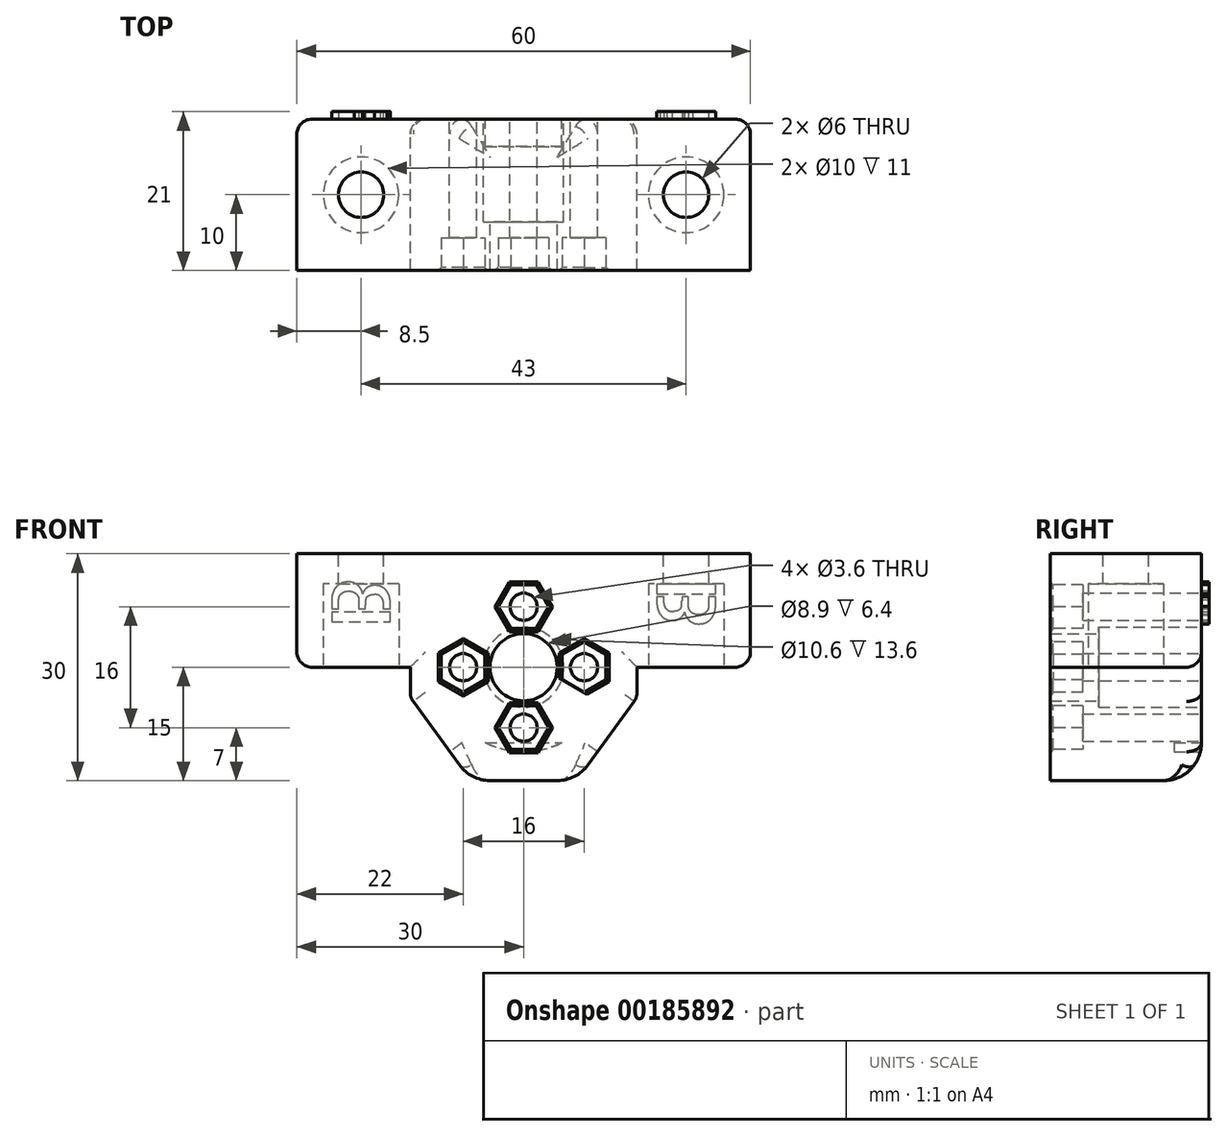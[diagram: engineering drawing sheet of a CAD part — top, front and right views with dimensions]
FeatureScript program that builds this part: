
annotation { "Feature Type Name" : "Feature", "Feature Type Description" : "" }
export const myFeature = defineFeature(function(context is Context, id is Id, definition is map)
    precondition{}
    {
        {
            var Q0;
            Q0=qCreatedBy(makeId("Front.planeOp"),FACE);
            var sketch = newSketch(context, id + "F0", { "sketchPlane" : qUnion([Q0])});
            skLineSegment(sketch, "E0.bottom", {"start": v(30, -7.5) * mm, "end": v(-30, -7.5) * mm});
            skLineSegment(sketch, "E0.top", {"start": v(30, 7.5) * mm, "end": v(-30, 7.5) * mm});
            skLineSegment(sketch, "E0.left", {"start": v(30, -7.5) * mm, "end": v(30, 7.5) * mm});
            skLineSegment(sketch, "E0.right", {"start": v(-30, -7.5) * mm, "end": v(-30, 7.5) * mm});
            skPoint(sketch, "E0.middle", {"position": v(0, 0) * mm});
            skLineSegment(sketch, "E1.bottom", {"start": v(-15, -7.5) * mm, "end": v(15, -7.5) * mm});
            skLineSegment(sketch, "E1.top", {"start": v(-15, -22.5) * mm, "end": v(15, -22.5) * mm});
            skLineSegment(sketch, "E1.left", {"start": v(-15, -7.5) * mm, "end": v(-15, -22.5) * mm});
            skLineSegment(sketch, "E1.right", {"start": v(15, -7.5) * mm, "end": v(15, -22.5) * mm});
            skPoint(sketch, "E2", {"position": v(0, -7.5) * mm});
            skCircle(sketch, "E3", {"center": v(0, -7.5) * mm, "radius": 4.45 * mm});
            skLineSegment(sketch, "E4", {"start": v(-7, -22.5) * mm, "end": v(-15, -11.5) * mm});
            skLineSegment(sketch, "E5.MirrorCS", {"start": v(7, -22.5) * mm, "end": v(15, -11.5) * mm});
            skLineSegment(sketch, "E6.MirrorCS", {"start": v(15, -22.5) * mm, "end": v(-15, -22.5) * mm});
            skSolve(sketch);
        }
        {
            var Q0;
            {var subQ10=sQuery(id+"F0.wireOp",EDGE,"E4");Q0=makeQuery(id+"F0.imprint","IMPRINT",FACE,{"disambiguationData":[TD([[makeQuery(id+"F0.imprint","IMPRINT",EDGE,{"derivedFrom":subQ10}),-1.0]])]});}
            var Q1;
            Q1=makeQuery(id+"F0.imprint","IMPRINT",FACE,{"disambiguationData":[TD([[makeQuery(id+"F0.imprint","IMPRINT",EDGE,{"derivedFrom":sQuery(id+"F0.wireOp",EDGE,"E0.top")}),1.0]])]});
            extrude(context, id + "F1", {"entities" : qUnion([Q0, Q1]), "depth" : 20 * mm});
        }
        {
            var Q0;
            Q0=makeQuery(id+"F1.opExtrude","SWEPT_FACE",FACE,{"disambiguationData":[OSD([sQuery(id+"F0.wireOp",EDGE,"E0.top")])]});
            var sketch = newSketch(context, id + "F2", { "sketchPlane" : qUnion([Q0])});
            skCircle(sketch, "E7", {"center": v(-21.5, -10) * mm, "radius": 3 * mm});
            skCircle(sketch, "E8.MirrorC", {"center": v(21.5, -10) * mm, "radius": 3 * mm});
            skSolve(sketch);
        }
        {
            var Q0;
            Q0 = qSketchRegion(id + "F2", true);
            extrude(context, id + "F3", {"entities" : qUnion([Q0]), "operationType" : NewBodyOperationType.REMOVE, "endBound" : BoundingType.UP_TO_NEXT, "oppositeDirection" : true, "depth" : 25 * mm});
        }
        {
            var Q0;
            {var subQ0=sQuery(id+"F0.wireOp",EDGE,"E0.bottom");Q0=makeQuery(id+"F1.opExtrude","SWEPT_FACE",FACE,{"disambiguationData":[OSD([subQ0]),TDD([makeQuery(id+"F0.imprint","IMPRINT",EDGE,{"disambiguationData":[TD([[makeQuery(id+"F0.imprint","INTERSECT",VERTEX,{"derivedFrom":[subQ0,sQuery(id+"F0.wireOp",EDGE,"E0.right")]}),1.0]])],"derivedFrom":subQ0})])]});}
            var sketch = newSketch(context, id + "F4", { "sketchPlane" : qUnion([Q0])});
            skCircle(sketch, "E9", {"center": v(-21.5, 10) * mm, "radius": 5 * mm});
            skCircle(sketch, "E10.MirrorC", {"center": v(21.5, 10) * mm, "radius": 5 * mm});
            skSolve(sketch);
        }
        {
            var Q0;
            Q0 = qSketchRegion(id + "F4", true);
            extrude(context, id + "F5", {"entities" : qUnion([Q0]), "operationType" : NewBodyOperationType.REMOVE, "oppositeDirection" : true, "depth" : 11 * mm});
        }
        {
            var Q0;
            {var subQ0=sQuery(id+"F0.wireOp",EDGE,"E0.bottom");Q0=makeQuery(id+"F1.opExtrude","CAP_EDGE",EDGE,{"disambiguationData":[OSD([subQ0]),TDD([makeQuery(id+"F0.imprint","IMPRINT",EDGE,{"disambiguationData":[TD([[makeQuery(id+"F0.imprint","INTERSECT",VERTEX,{"derivedFrom":[subQ0,sQuery(id+"F0.wireOp",EDGE,"E0.right")]}),1.0]])],"derivedFrom":subQ0})])],"isStart":true});}
            var Q1;
            Q1=makeQuery(id+"F1.opExtrude","CAP_EDGE",EDGE,{"disambiguationData":[OSD([sQuery(id+"F0.wireOp",EDGE,"E0.right")])],"isStart":true});
            var Q2;
            Q2=makeQuery(id+"F1.opExtrude","CAP_EDGE",EDGE,{"disambiguationData":[OSD([sQuery(id+"F0.wireOp",EDGE,"E1.left")])],"isStart":true});
            var Q3;
            Q3=makeQuery(id+"F1.opExtrude","CAP_EDGE",EDGE,{"disambiguationData":[OSD([sQuery(id+"F0.wireOp",EDGE,"E4")])],"isStart":true});
            var Q4;
            Q4=makeQuery(id+"F1.opExtrude","CAP_EDGE",EDGE,{"disambiguationData":[OSD([sQuery(id+"F0.wireOp",EDGE,"E6.MirrorCS")])],"isStart":true});
            var Q5;
            Q5=makeQuery(id+"F1.opExtrude","CAP_EDGE",EDGE,{"disambiguationData":[OSD([sQuery(id+"F0.wireOp",EDGE,"E5.MirrorCS")])],"isStart":true});
            var Q6;
            Q6=makeQuery(id+"F1.opExtrude","CAP_EDGE",EDGE,{"disambiguationData":[OSD([sQuery(id+"F0.wireOp",EDGE,"E1.right")])],"isStart":true});
            var Q7;
            {var subQ0=sQuery(id+"F0.wireOp",EDGE,"E0.bottom");Q7=makeQuery(id+"F1.opExtrude","CAP_EDGE",EDGE,{"disambiguationData":[OSD([subQ0]),TDD([makeQuery(id+"F0.imprint","IMPRINT",EDGE,{"disambiguationData":[TD([[makeQuery(id+"F0.imprint","INTERSECT",VERTEX,{"derivedFrom":[subQ0,sQuery(id+"F0.wireOp",EDGE,"E0.left")]}),-1.0]])],"derivedFrom":subQ0})])],"isStart":true});}
            var Q8;
            Q8=makeQuery(id+"F1.opExtrude","CAP_EDGE",EDGE,{"disambiguationData":[OSD([sQuery(id+"F0.wireOp",EDGE,"E0.left")])],"isStart":true});
            var Q9;
            Q9=makeQuery(id+"F1.opExtrude","SWEPT_EDGE",EDGE,{"disambiguationData":[OSD([sQuery(id+"F0.wireOp",EDGE,"E1.right"),sQuery(id+"F0.wireOp",EDGE,"E5.MirrorCS")])]});
            var Q10;
            Q10=makeQuery(id+"F1.opExtrude","SWEPT_EDGE",EDGE,{"disambiguationData":[OSD([sQuery(id+"F0.wireOp",EDGE,"E1.left"),sQuery(id+"F0.wireOp",EDGE,"E4")])]});
            var Q11;
            Q11=makeQuery(id+"F1.opExtrude","SWEPT_EDGE",EDGE,{"disambiguationData":[OSD([sQuery(id+"F0.wireOp",EDGE,"E0.bottom"),sQuery(id+"F0.wireOp",EDGE,"E0.right")])]});
            var Q12;
            Q12=makeQuery(id+"F1.opExtrude","SWEPT_EDGE",EDGE,{"disambiguationData":[OSD([sQuery(id+"F0.wireOp",EDGE,"E0.bottom"),sQuery(id+"F0.wireOp",EDGE,"E0.left")])]});
            fillet(context, id + "F6", {"entities" : qUnion([Q0, Q1, Q2, Q3, Q4, Q5, Q6, Q7, Q8, Q9, Q10, Q11, Q12]), "radius" : 2 * mm, "tangentPropagation" : true});
        }
        {
            var Q0;
            Q0=makeQuery(id+"F1.opExtrude","SWEPT_EDGE",EDGE,{"disambiguationData":[OSD([sQuery(id+"F0.wireOp",EDGE,"E4"),sQuery(id+"F0.wireOp",EDGE,"E6.MirrorCS")])]});
            var Q1;
            Q1=makeQuery(id+"F1.opExtrude","SWEPT_EDGE",EDGE,{"disambiguationData":[OSD([sQuery(id+"F0.wireOp",EDGE,"E5.MirrorCS"),sQuery(id+"F0.wireOp",EDGE,"E6.MirrorCS")])]});
            fillet(context, id + "F7", {"entities" : qUnion([Q0, Q1]), "radius" : 5 * mm, "tangentPropagation" : true});
        }
        {
            var Q0;
            Q0=makeQuery(id+"F1.opExtrude","CAP_FACE",FACE,{"disambiguationData":[OSD([sQuery(id+"F0.wireOp",EDGE,"E0.bottom"),sQuery(id+"F0.wireOp",EDGE,"E0.top"),sQuery(id+"F0.wireOp",EDGE,"E0.left"),sQuery(id+"F0.wireOp",EDGE,"E0.right"),sQuery(id+"F0.wireOp",EDGE,"E1.left"),sQuery(id+"F0.wireOp",EDGE,"E3"),sQuery(id+"F0.wireOp",EDGE,"E4"),sQuery(id+"F0.wireOp",EDGE,"E1.right"),sQuery(id+"F0.wireOp",EDGE,"E5.MirrorCS"),sQuery(id+"F0.wireOp",EDGE,"E6.MirrorCS")])],"isStart":true});
            var sketch = newSketch(context, id + "F8", { "sketchPlane" : qUnion([Q0])});
            skCircle(sketch, "E11", {"center": v(0, -7.5) * mm, "radius": 11.2 * mm});
            skCircle(sketch, "E12", {"center": v(0, -7.5) * mm, "radius": 5.3 * mm});
            skCircle(sketch, "E13", {"center": v(8, -7.5) * mm, "radius": 1.8 * mm});
            skCircle(sketch, "E14.1.0", {"center": v(0, 0.5) * mm, "radius": 1.8 * mm});
            skCircle(sketch, "E14.2.0", {"center": v(-8, -7.5) * mm, "radius": 1.8 * mm});
            skCircle(sketch, "E14.3.0", {"center": v(0, -15.5) * mm, "radius": 1.8 * mm});
            skCircle(sketch, "E15", {"center": v(0, -7.5) * mm, "radius": 8 * mm, "construction": true});
            skSolve(sketch);
        }
        {
            var Q0;
            Q0=makeQuery(id+"F8.imprint","IMPRINT",FACE,{"disambiguationData":[TD([[makeQuery(id+"F8.imprint","IMPRINT",EDGE,{"derivedFrom":sQuery(id+"F8.wireOp",EDGE,"E12")}),1.0]])]});
            var Q1;
            Q1=makeQuery(id+"F8.imprint","IMPRINT",FACE,{"disambiguationData":[TD([[makeQuery(id+"F8.imprint","IMPRINT",EDGE,{"derivedFrom":makeQuery(id+"F1.opExtrude","CAP_EDGE",EDGE,{"disambiguationData":[OSD([sQuery(id+"F0.wireOp",EDGE,"E3")])],"isStart":true})}),-1.0]])]});
            extrude(context, id + "F9", {"entities" : qUnion([Q0, Q1]), "operationType" : NewBodyOperationType.REMOVE, "oppositeDirection" : true, "depth" : (3.6 + 10) * mm});
        }
        {
            var Q0;
            Q0=makeQuery(id+"F8.imprint","IMPRINT",FACE,{"disambiguationData":[TD([[makeQuery(id+"F8.imprint","IMPRINT",EDGE,{"derivedFrom":sQuery(id+"F8.wireOp",EDGE,"E11")}),1.0]])]});
            var Q1;
            Q1=makeQuery(id+"F8.imprint","IMPRINT",FACE,{"disambiguationData":[TD([[makeQuery(id+"F8.imprint","IMPRINT",EDGE,{"derivedFrom":sQuery(id+"F8.wireOp",EDGE,"E13")}),1.0]])]});
            var Q2;
            Q2=makeQuery(id+"F8.imprint","IMPRINT",FACE,{"disambiguationData":[TD([[makeQuery(id+"F8.imprint","IMPRINT",EDGE,{"derivedFrom":sQuery(id+"F8.wireOp",EDGE,"E14.3.0")}),1.0]])]});
            var Q3;
            Q3=makeQuery(id+"F8.imprint","IMPRINT",FACE,{"disambiguationData":[TD([[makeQuery(id+"F8.imprint","IMPRINT",EDGE,{"derivedFrom":sQuery(id+"F8.wireOp",EDGE,"E14.2.0")}),1.0]])]});
            var Q4;
            Q4=makeQuery(id+"F8.imprint","IMPRINT",FACE,{"disambiguationData":[TD([[makeQuery(id+"F8.imprint","IMPRINT",EDGE,{"derivedFrom":sQuery(id+"F8.wireOp",EDGE,"E14.1.0")}),1.0]])]});
            extrude(context, id + "F10", {"entities" : qUnion([Q0, Q1, Q2, Q3, Q4]), "operationType" : NewBodyOperationType.REMOVE, "oppositeDirection" : true, "depth" : (3.5 + .1) * mm});
        }
        {
            var Q0;
            Q0=makeQuery(id+"F8.imprint","IMPRINT",FACE,{"disambiguationData":[TD([[makeQuery(id+"F8.imprint","IMPRINT",EDGE,{"derivedFrom":sQuery(id+"F8.wireOp",EDGE,"E13")}),1.0]])]});
            var Q1;
            Q1=makeQuery(id+"F8.imprint","IMPRINT",FACE,{"disambiguationData":[TD([[makeQuery(id+"F8.imprint","IMPRINT",EDGE,{"derivedFrom":sQuery(id+"F8.wireOp",EDGE,"E14.3.0")}),1.0]])]});
            var Q2;
            Q2=makeQuery(id+"F8.imprint","IMPRINT",FACE,{"disambiguationData":[TD([[makeQuery(id+"F8.imprint","IMPRINT",EDGE,{"derivedFrom":sQuery(id+"F8.wireOp",EDGE,"E14.2.0")}),1.0]])]});
            var Q3;
            Q3=makeQuery(id+"F8.imprint","IMPRINT",FACE,{"disambiguationData":[TD([[makeQuery(id+"F8.imprint","IMPRINT",EDGE,{"derivedFrom":sQuery(id+"F8.wireOp",EDGE,"E14.1.0")}),1.0]])]});
            var Q4;
            Q4=makeQuery(id+"F1.opExtrude","CAP_FACE",FACE,{"disambiguationData":[OSD([sQuery(id+"F0.wireOp",EDGE,"E0.bottom"),sQuery(id+"F0.wireOp",EDGE,"E0.top"),sQuery(id+"F0.wireOp",EDGE,"E0.left"),sQuery(id+"F0.wireOp",EDGE,"E0.right"),sQuery(id+"F0.wireOp",EDGE,"E1.left"),sQuery(id+"F0.wireOp",EDGE,"E3"),sQuery(id+"F0.wireOp",EDGE,"E4"),sQuery(id+"F0.wireOp",EDGE,"E1.right"),sQuery(id+"F0.wireOp",EDGE,"E5.MirrorCS"),sQuery(id+"F0.wireOp",EDGE,"E6.MirrorCS")])],"isStart":false});
            extrude(context, id + "F11", {"entities" : qUnion([Q0, Q1, Q2, Q3]), "operationType" : NewBodyOperationType.REMOVE, "endBound" : BoundingType.UP_TO_SURFACE, "oppositeDirection" : true, "endBoundEntityFace" : qUnion([Q4]), "depth" : 25 * mm});
        }
        {
            var Q0;
            Q0=makeQuery(id+"F1.opExtrude","CAP_FACE",FACE,{"disambiguationData":[OSD([sQuery(id+"F0.wireOp",EDGE,"E0.bottom"),sQuery(id+"F0.wireOp",EDGE,"E0.top"),sQuery(id+"F0.wireOp",EDGE,"E0.left"),sQuery(id+"F0.wireOp",EDGE,"E0.right"),sQuery(id+"F0.wireOp",EDGE,"E1.left"),sQuery(id+"F0.wireOp",EDGE,"E3"),sQuery(id+"F0.wireOp",EDGE,"E4"),sQuery(id+"F0.wireOp",EDGE,"E1.right"),sQuery(id+"F0.wireOp",EDGE,"E5.MirrorCS"),sQuery(id+"F0.wireOp",EDGE,"E6.MirrorCS")])],"isStart":true});
            var sketch = newSketch(context, id + "F12", { "sketchPlane" : qUnion([Q0])});
            skText(sketch, "E16", { "text": "B", "fontName": "AllertaStencil-Regular.ttf"});
            skLineSegment(sketch, "E17", {"start": v(21.5, 4.5) * mm, "end": v(21.5, -2.5) * mm, "construction": true});
            skLineSegment(sketch, "E18.MirrorCS", {"start": v(-21.5, 4.5) * mm, "end": v(-21.5, -2.5) * mm, "construction": true});
            skText(sketch, "E19", { "text": "B", "fontName": "AllertaStencil-Regular.ttf"});
            skLineSegment(sketch, "E20", {"start": v(-21.5, -2.5) * mm, "end": v(-21.5, 4.5) * mm, "construction": true});
            const initialGuessF12  = {"E16": [0.0254, -0.0025, 0, 1, 0.00779], "E19": [-0.0254, 0.0045, 0, -1, 0.00779]};
            skSetInitialGuess(sketch, initialGuessF12);
            skSolve(sketch);
        }
        {
            var Q0;
            Q0 = qSketchRegion(id + "F12", true);
            extrude(context, id + "F13", {"entities" : qUnion([Q0]), "operationType" : NewBodyOperationType.ADD, "depth" : 1 * mm});
        }
        {
            var Q0;
            Q0=makeQuery(id+"F1.opExtrude","CAP_FACE",FACE,{"disambiguationData":[OSD([sQuery(id+"F0.wireOp",EDGE,"E0.bottom"),sQuery(id+"F0.wireOp",EDGE,"E0.top"),sQuery(id+"F0.wireOp",EDGE,"E0.left"),sQuery(id+"F0.wireOp",EDGE,"E0.right"),sQuery(id+"F0.wireOp",EDGE,"E1.left"),sQuery(id+"F0.wireOp",EDGE,"E3"),sQuery(id+"F0.wireOp",EDGE,"E4"),sQuery(id+"F0.wireOp",EDGE,"E1.right"),sQuery(id+"F0.wireOp",EDGE,"E5.MirrorCS"),sQuery(id+"F0.wireOp",EDGE,"E6.MirrorCS")])],"isStart":false});
            var sketch = newSketch(context, id + "F14", { "sketchPlane" : qUnion([Q0])});
            skCircle(sketch, "E21.cCircle", {"center": v(0, -15.5) * mm, "radius": 2.9 * mm, "construction": true});
            skLineSegment(sketch, "E21.0", {"start": v(-1.67, -18.4) * mm, "end": v(-3.35, -15.5) * mm});
            skLineSegment(sketch, "E21.1", {"start": v(-3.35, -15.5) * mm, "end": v(-1.67, -12.6) * mm});
            skLineSegment(sketch, "E21.2", {"start": v(-1.67, -12.6) * mm, "end": v(1.67, -12.6) * mm});
            skLineSegment(sketch, "E21.3", {"start": v(1.67, -12.6) * mm, "end": v(3.35, -15.5) * mm});
            skLineSegment(sketch, "E21.4", {"start": v(3.35, -15.5) * mm, "end": v(1.67, -18.4) * mm});
            skLineSegment(sketch, "E21.5", {"start": v(1.67, -18.4) * mm, "end": v(-1.67, -18.4) * mm});
            skPoint(sketch, "E21.0.midPoint", {"position": v(-2.51, -16.95) * mm});
            skLineSegment(sketch, "E22", {"start": v(0, 0) * mm, "end": v(16.56, 0) * mm, "construction": true});
            skLineSegment(sketch, "E23.1.0", {"start": v(10.9, -5.83) * mm, "end": v(10.9, -9.17) * mm});
            skLineSegment(sketch, "E23.1.1", {"start": v(5.1, -9.17) * mm, "end": v(5.1, -5.83) * mm});
            skLineSegment(sketch, "E23.1.2", {"start": v(5.1, -5.83) * mm, "end": v(8, -4.15) * mm});
            skLineSegment(sketch, "E23.1.3", {"start": v(8, -10.85) * mm, "end": v(5.1, -9.17) * mm});
            skLineSegment(sketch, "E23.1.4", {"start": v(8, -4.15) * mm, "end": v(10.9, -5.83) * mm});
            skLineSegment(sketch, "E23.1.5", {"start": v(10.9, -9.17) * mm, "end": v(8, -10.85) * mm});
            skCircle(sketch, "E23.1.6", {"center": v(8, -7.5) * mm, "radius": 2.9 * mm, "construction": true});
            skPoint(sketch, "E23.1.7", {"position": v(9.45, -10.01) * mm});
            skLineSegment(sketch, "E23.2.0", {"start": v(-1.67, 3.4) * mm, "end": v(1.67, 3.4) * mm});
            skLineSegment(sketch, "E23.2.1", {"start": v(1.67, -2.4) * mm, "end": v(-1.67, -2.4) * mm});
            skLineSegment(sketch, "E23.2.2", {"start": v(-1.67, -2.4) * mm, "end": v(-3.35, 0.5) * mm});
            skLineSegment(sketch, "E23.2.3", {"start": v(3.35, 0.5) * mm, "end": v(1.67, -2.4) * mm});
            skLineSegment(sketch, "E23.2.4", {"start": v(-3.35, 0.5) * mm, "end": v(-1.67, 3.4) * mm});
            skLineSegment(sketch, "E23.2.5", {"start": v(1.67, 3.4) * mm, "end": v(3.35, 0.5) * mm});
            skCircle(sketch, "E23.2.6", {"center": v(0, 0.5) * mm, "radius": 2.9 * mm, "construction": true});
            skPoint(sketch, "E23.2.7", {"position": v(2.51, 1.95) * mm});
            skLineSegment(sketch, "E23.3.0", {"start": v(-10.9, -9.17) * mm, "end": v(-10.9, -5.83) * mm});
            skLineSegment(sketch, "E23.3.1", {"start": v(-5.1, -5.83) * mm, "end": v(-5.1, -9.17) * mm});
            skLineSegment(sketch, "E23.3.2", {"start": v(-5.1, -9.17) * mm, "end": v(-8, -10.85) * mm});
            skLineSegment(sketch, "E23.3.3", {"start": v(-8, -4.15) * mm, "end": v(-5.1, -5.83) * mm});
            skLineSegment(sketch, "E23.3.4", {"start": v(-8, -10.85) * mm, "end": v(-10.9, -9.17) * mm});
            skLineSegment(sketch, "E23.3.5", {"start": v(-10.9, -5.83) * mm, "end": v(-8, -4.15) * mm});
            skCircle(sketch, "E23.3.6", {"center": v(-8, -7.5) * mm, "radius": 2.9 * mm, "construction": true});
            skPoint(sketch, "E23.3.7", {"position": v(-9.45, -4.99) * mm});
            skPoint(sketch, "E23.center", {"position": v(0, -7.5) * mm});
            skSolve(sketch);
        }
        {
            var Q0;
            Q0 = qSketchRegion(id + "F14", true);
            extrude(context, id + "F15", {"entities" : qUnion([Q0]), "operationType" : NewBodyOperationType.REMOVE, "oppositeDirection" : true, "depth" : (4 + .3) * mm});
        }
        {
            var Q0;
            Q0=makeQuery(id+"F15.boolean.opBoolean","COPY",EDGE,{"derivedFrom":makeQuery(id+"F15.opExtrude","CAP_EDGE",EDGE,{"disambiguationData":[OSD([sQuery(id+"F14.wireOp",EDGE,"E23.3.0")])],"isStart":true})});
            var Q1;
            Q1=makeQuery(id+"F15.boolean.opBoolean","COPY",EDGE,{"derivedFrom":makeQuery(id+"F15.opExtrude","CAP_EDGE",EDGE,{"disambiguationData":[OSD([sQuery(id+"F14.wireOp",EDGE,"E23.3.5")])],"isStart":true})});
            var Q2;
            Q2=makeQuery(id+"F15.boolean.opBoolean","COPY",EDGE,{"derivedFrom":makeQuery(id+"F15.opExtrude","CAP_EDGE",EDGE,{"disambiguationData":[OSD([sQuery(id+"F14.wireOp",EDGE,"E23.3.3")])],"isStart":true})});
            var Q3;
            Q3=makeQuery(id+"F15.boolean.opBoolean","COPY",EDGE,{"derivedFrom":makeQuery(id+"F15.opExtrude","CAP_EDGE",EDGE,{"disambiguationData":[OSD([sQuery(id+"F14.wireOp",EDGE,"E23.3.1")])],"isStart":true})});
            var Q4;
            Q4=makeQuery(id+"F15.boolean.opBoolean","COPY",EDGE,{"derivedFrom":makeQuery(id+"F15.opExtrude","CAP_EDGE",EDGE,{"disambiguationData":[OSD([sQuery(id+"F14.wireOp",EDGE,"E23.3.2")])],"isStart":true})});
            var Q5;
            Q5=makeQuery(id+"F15.boolean.opBoolean","COPY",EDGE,{"derivedFrom":makeQuery(id+"F15.opExtrude","CAP_EDGE",EDGE,{"disambiguationData":[OSD([sQuery(id+"F14.wireOp",EDGE,"E23.3.4")])],"isStart":true})});
            var Q6;
            Q6=makeQuery(id+"F15.boolean.opBoolean","COPY",EDGE,{"derivedFrom":makeQuery(id+"F15.opExtrude","CAP_EDGE",EDGE,{"disambiguationData":[OSD([sQuery(id+"F14.wireOp",EDGE,"E21.1")])],"isStart":true})});
            var Q7;
            Q7=makeQuery(id+"F15.boolean.opBoolean","COPY",EDGE,{"derivedFrom":makeQuery(id+"F15.opExtrude","CAP_EDGE",EDGE,{"disambiguationData":[OSD([sQuery(id+"F14.wireOp",EDGE,"E21.2")])],"isStart":true})});
            var Q8;
            Q8=makeQuery(id+"F15.boolean.opBoolean","COPY",EDGE,{"derivedFrom":makeQuery(id+"F15.opExtrude","CAP_EDGE",EDGE,{"disambiguationData":[OSD([sQuery(id+"F14.wireOp",EDGE,"E21.3")])],"isStart":true})});
            var Q9;
            Q9=makeQuery(id+"F15.boolean.opBoolean","COPY",EDGE,{"derivedFrom":makeQuery(id+"F15.opExtrude","CAP_EDGE",EDGE,{"disambiguationData":[OSD([sQuery(id+"F14.wireOp",EDGE,"E21.4")])],"isStart":true})});
            var Q10;
            Q10=makeQuery(id+"F15.boolean.opBoolean","COPY",EDGE,{"derivedFrom":makeQuery(id+"F15.opExtrude","CAP_EDGE",EDGE,{"disambiguationData":[OSD([sQuery(id+"F14.wireOp",EDGE,"E21.5")])],"isStart":true})});
            var Q11;
            Q11=makeQuery(id+"F15.boolean.opBoolean","COPY",EDGE,{"derivedFrom":makeQuery(id+"F15.opExtrude","CAP_EDGE",EDGE,{"disambiguationData":[OSD([sQuery(id+"F14.wireOp",EDGE,"E21.0")])],"isStart":true})});
            var Q12;
            Q12=makeQuery(id+"F15.boolean.opBoolean","COPY",EDGE,{"derivedFrom":makeQuery(id+"F15.opExtrude","CAP_EDGE",EDGE,{"disambiguationData":[OSD([sQuery(id+"F14.wireOp",EDGE,"E23.1.1")])],"isStart":true})});
            var Q13;
            Q13=makeQuery(id+"F15.boolean.opBoolean","COPY",EDGE,{"derivedFrom":makeQuery(id+"F15.opExtrude","CAP_EDGE",EDGE,{"disambiguationData":[OSD([sQuery(id+"F14.wireOp",EDGE,"E23.1.2")])],"isStart":true})});
            var Q14;
            Q14=makeQuery(id+"F15.boolean.opBoolean","COPY",EDGE,{"derivedFrom":makeQuery(id+"F15.opExtrude","CAP_EDGE",EDGE,{"disambiguationData":[OSD([sQuery(id+"F14.wireOp",EDGE,"E23.1.4")])],"isStart":true})});
            var Q15;
            Q15=makeQuery(id+"F15.boolean.opBoolean","COPY",EDGE,{"derivedFrom":makeQuery(id+"F15.opExtrude","CAP_EDGE",EDGE,{"disambiguationData":[OSD([sQuery(id+"F14.wireOp",EDGE,"E23.1.0")])],"isStart":true})});
            var Q16;
            Q16=makeQuery(id+"F15.boolean.opBoolean","COPY",EDGE,{"derivedFrom":makeQuery(id+"F15.opExtrude","CAP_EDGE",EDGE,{"disambiguationData":[OSD([sQuery(id+"F14.wireOp",EDGE,"E23.1.5")])],"isStart":true})});
            var Q17;
            Q17=makeQuery(id+"F15.boolean.opBoolean","COPY",EDGE,{"derivedFrom":makeQuery(id+"F15.opExtrude","CAP_EDGE",EDGE,{"disambiguationData":[OSD([sQuery(id+"F14.wireOp",EDGE,"E23.2.1")])],"isStart":true})});
            var Q18;
            Q18=makeQuery(id+"F15.boolean.opBoolean","COPY",EDGE,{"derivedFrom":makeQuery(id+"F15.opExtrude","CAP_EDGE",EDGE,{"disambiguationData":[OSD([sQuery(id+"F14.wireOp",EDGE,"E23.2.4")])],"isStart":true})});
            var Q19;
            Q19=makeQuery(id+"F15.boolean.opBoolean","COPY",EDGE,{"derivedFrom":makeQuery(id+"F15.opExtrude","CAP_EDGE",EDGE,{"disambiguationData":[OSD([sQuery(id+"F14.wireOp",EDGE,"E23.2.3")])],"isStart":true})});
            var Q20;
            Q20=makeQuery(id+"F15.boolean.opBoolean","COPY",EDGE,{"derivedFrom":makeQuery(id+"F15.opExtrude","CAP_EDGE",EDGE,{"disambiguationData":[OSD([sQuery(id+"F14.wireOp",EDGE,"E23.2.0")])],"isStart":true})});
            var Q21;
            Q21=makeQuery(id+"F15.boolean.opBoolean","COPY",EDGE,{"derivedFrom":makeQuery(id+"F15.opExtrude","CAP_EDGE",EDGE,{"disambiguationData":[OSD([sQuery(id+"F14.wireOp",EDGE,"E23.2.5")])],"isStart":true})});
            var Q22;
            Q22=makeQuery(id+"F15.boolean.opBoolean","COPY",EDGE,{"derivedFrom":makeQuery(id+"F15.opExtrude","CAP_EDGE",EDGE,{"disambiguationData":[OSD([sQuery(id+"F14.wireOp",EDGE,"E23.2.2")])],"isStart":true})});
            var Q23;
            Q23=makeQuery(id+"F10.boolean.opBoolean","COPY",EDGE,{"derivedFrom":makeQuery(id+"F10.opExtrude","CAP_EDGE",EDGE,{"disambiguationData":[OSD([sQuery(id+"F8.wireOp",EDGE,"E12")])],"isStart":false})});
            chamfer(context, id + "F16", {"entities" : qUnion([Q0, Q1, Q2, Q3, Q4, Q5, Q6, Q7, Q8, Q9, Q10, Q11, Q12, Q13, Q14, Q15, Q16, Q17, Q18, Q19, Q20, Q21, Q22, Q23]), "width" : .4 * mm, "tangentPropagation" : true});
        }
    });
